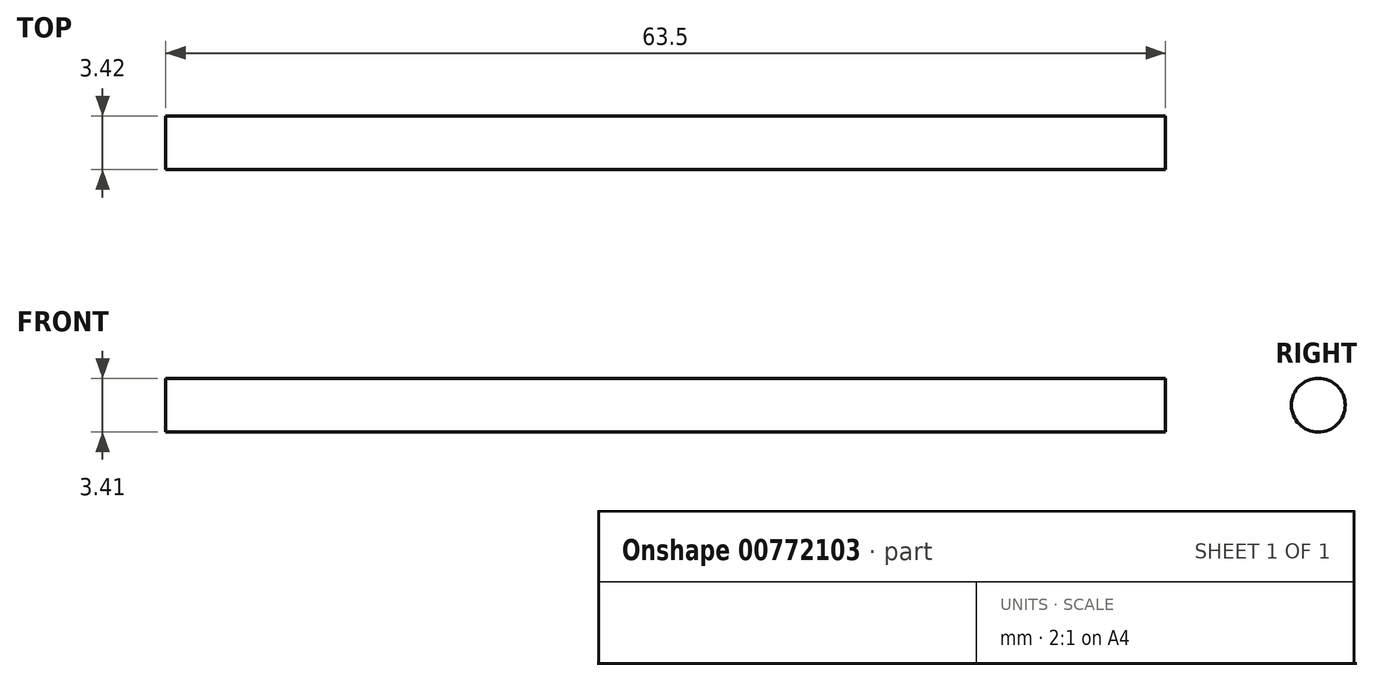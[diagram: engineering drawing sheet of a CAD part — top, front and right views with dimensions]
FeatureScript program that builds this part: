
annotation { "Feature Type Name" : "Feature", "Feature Type Description" : "" }
export const myFeature = defineFeature(function(context is Context, id is Id, definition is map)
    precondition{}
    {
        {
            var Q0;
            Q0=qCreatedBy(makeId("Front.planeOp"),FACE);
            var sketch = newSketch(context, id + "F0", { "sketchPlane" : qUnion([Q0])});
            skLineSegment(sketch, "E0", {"start": v(0, 0) * mm, "end": v(-63.5, 0) * mm});
            skLineSegment(sketch, "E1", {"start": v(-63.5, 0) * mm, "end": v(-63.5, 1.7) * mm});
            skLineSegment(sketch, "E2", {"start": v(-63.5, 1.7) * mm, "end": v(0, 1.7) * mm});
            skLineSegment(sketch, "E3", {"start": v(0, 1.7) * mm, "end": v(0, 0) * mm});
            skSolve(sketch);
        }
        {
            var Q0;
            Q0=makeQuery(id+"F0.imprint","IMPRINT",FACE,{"disambiguationData":[TD([[makeQuery(id+"F0.imprint","IMPRINT",EDGE,{"derivedFrom":sQuery(id+"F0.wireOp",EDGE,"E0")}),-1.0]])]});
            var Q1;
            Q1=sQuery(id+"F0.wireOp",EDGE,"E2");
            revolve(context, id + "F1", {"surfaceOperationType" : NewSurfaceOperationType.NEW, "entities" : qUnion([Q0]), "axis" : qUnion([Q1]), "revolveType" : RevolveType.FULL});
        }
    });
